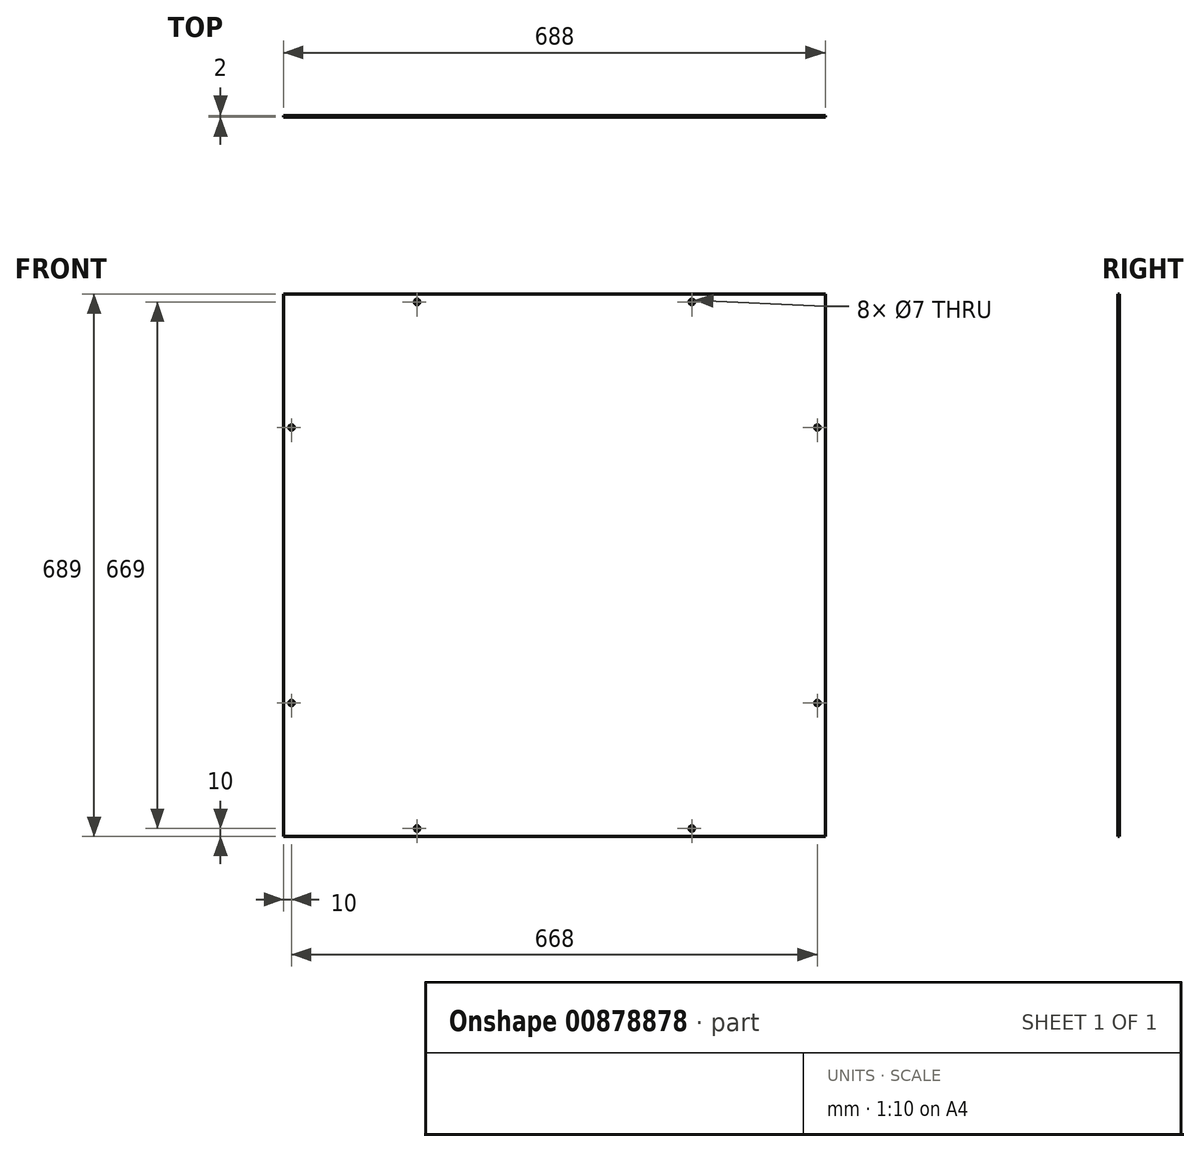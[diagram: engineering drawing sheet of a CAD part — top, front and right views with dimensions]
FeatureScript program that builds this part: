
annotation { "Feature Type Name" : "Feature", "Feature Type Description" : "" }
export const myFeature = defineFeature(function(context is Context, id is Id, definition is map)
    precondition{}
    {
        {
            var Q0;
            Q0=qCreatedBy(makeId("Front.planeOp"),FACE);
            var sketch = newSketch(context, id + "F0", { "sketchPlane" : qUnion([Q0])});
            skLineSegment(sketch, "E0.bottom", {"start": v(0, 0) * mm, "end": v(688, 0) * mm});
            skLineSegment(sketch, "E0.top", {"start": v(0, 689) * mm, "end": v(688, 689) * mm});
            skLineSegment(sketch, "E0.left", {"start": v(0, 0) * mm, "end": v(0, 689) * mm});
            skLineSegment(sketch, "E0.right", {"start": v(688, 0) * mm, "end": v(688, 689) * mm});
            skSolve(sketch);
        }
        {
            var Q0;
            Q0=makeQuery(id+"F0.imprint","IMPRINT",FACE,{"disambiguationData":[TD([[makeQuery(id+"F0.imprint","IMPRINT",EDGE,{"derivedFrom":sQuery(id+"F0.wireOp",EDGE,"E0.bottom")}),1.0]])]});
            extrude(context, id + "F1", {"entities" : qUnion([Q0]), "depth" : 2 * mm, "offsetDistance" : 25 * mm});
        }
        {
            var Q0;
            Q0=makeQuery(id+"F1.opExtrude","CAP_FACE",FACE,{"disambiguationData":[OSD([sQuery(id+"F0.wireOp",EDGE,"E0.bottom"),sQuery(id+"F0.wireOp",EDGE,"E0.top"),sQuery(id+"F0.wireOp",EDGE,"E0.left"),sQuery(id+"F0.wireOp",EDGE,"E0.right")])],"isStart":false});
            var sketch = newSketch(context, id + "F2", { "sketchPlane" : qUnion([Q0])});
            skLineSegment(sketch, "E1", {"start": v(169.5, 689) * mm, "end": v(169.5, 0) * mm, "construction": true});
            skLineSegment(sketch, "E2", {"start": v(344, 689) * mm, "end": v(344, 0) * mm, "construction": true});
            skLineSegment(sketch, "E3", {"start": v(0, 344.5) * mm, "end": v(688, 344.5) * mm, "construction": true});
            skLineSegment(sketch, "E4", {"start": v(0, 519.5) * mm, "end": v(688, 519.5) * mm, "construction": true});
            skLineSegment(sketch, "E5.MirrorCS", {"start": v(518.5, 689) * mm, "end": v(518.5, 0) * mm, "construction": true});
            skLineSegment(sketch, "E6.MirrorCS", {"start": v(0, 169.5) * mm, "end": v(688, 169.5) * mm, "construction": true});
            skLineSegment(sketch, "E7", {"start": v(10, 689) * mm, "end": v(10, 0) * mm, "construction": true});
            skLineSegment(sketch, "E8", {"start": v(0, 679) * mm, "end": v(688, 679) * mm, "construction": true});
            skLineSegment(sketch, "E9.MirrorCS", {"start": v(0, 10) * mm, "end": v(688, 10) * mm, "construction": true});
            skLineSegment(sketch, "E10.MirrorCS", {"start": v(678, 689) * mm, "end": v(678, 0) * mm, "construction": true});
            skCircle(sketch, "E11", {"center": v(10, 519.5) * mm, "radius": 3.5 * mm});
            skCircle(sketch, "E12", {"center": v(169.5, 679) * mm, "radius": 3.5 * mm});
            skCircle(sketch, "E13.MirrorC", {"center": v(678, 519.5) * mm, "radius": 3.5 * mm});
            skCircle(sketch, "E14.MirrorC", {"center": v(518.5, 679) * mm, "radius": 3.5 * mm});
            skCircle(sketch, "E15.MirrorC", {"center": v(10, 169.5) * mm, "radius": 3.5 * mm});
            skCircle(sketch, "E16.MirrorC", {"center": v(169.5, 10) * mm, "radius": 3.5 * mm});
            skCircle(sketch, "E17.MirrorC", {"center": v(518.5, 10) * mm, "radius": 3.5 * mm});
            skCircle(sketch, "E18.MirrorC", {"center": v(678, 169.5) * mm, "radius": 3.5 * mm});
            skSolve(sketch);
        }
        {
            var Q0;
            Q0=sQuery(id+"F2.wireOp",VERTEX,"E12.center");
            var Q1;
            Q1=sQuery(id+"F2.wireOp",VERTEX,"E11.center");
            var Q2;
            Q2=sQuery(id+"F2.wireOp",VERTEX,"E14.MirrorC.center");
            var Q3;
            Q3=sQuery(id+"F2.wireOp",VERTEX,"E13.MirrorC.center");
            var Q4;
            Q4=sQuery(id+"F2.wireOp",VERTEX,"E18.MirrorC.center");
            var Q5;
            Q5=sQuery(id+"F2.wireOp",VERTEX,"E17.MirrorC.center");
            var Q6;
            Q6=sQuery(id+"F2.wireOp",VERTEX,"E16.MirrorC.center");
            var Q7;
            Q7=sQuery(id+"F2.wireOp",VERTEX,"E15.MirrorC.center");
            var Q8;
            Q8=makeQuery(id+"F1.opExtrude","SWEPT_BODY",BODY,{"disambiguationData":[OSD([sQuery(id+"F0.wireOp",EDGE,"E0.bottom"),sQuery(id+"F0.wireOp",EDGE,"E0.top"),sQuery(id+"F0.wireOp",EDGE,"E0.left"),sQuery(id+"F0.wireOp",EDGE,"E0.right")])]});
            hole(context, id + "F3", {"style" : HoleStyle.SIMPLE, "endStyle" : HoleEndStyle.THROUGH, "holeDiameter" : 7 * mm, "majorDiameter" : 5 * mm, "isTappedThrough" : true, "tappedDepth" : 12 * mm, "tapClearance" : 3, "locations" : qUnion([Q0, Q1, Q2, Q3, Q4, Q5, Q6, Q7]), "scope" : qUnion([Q8])});
        }
    });
